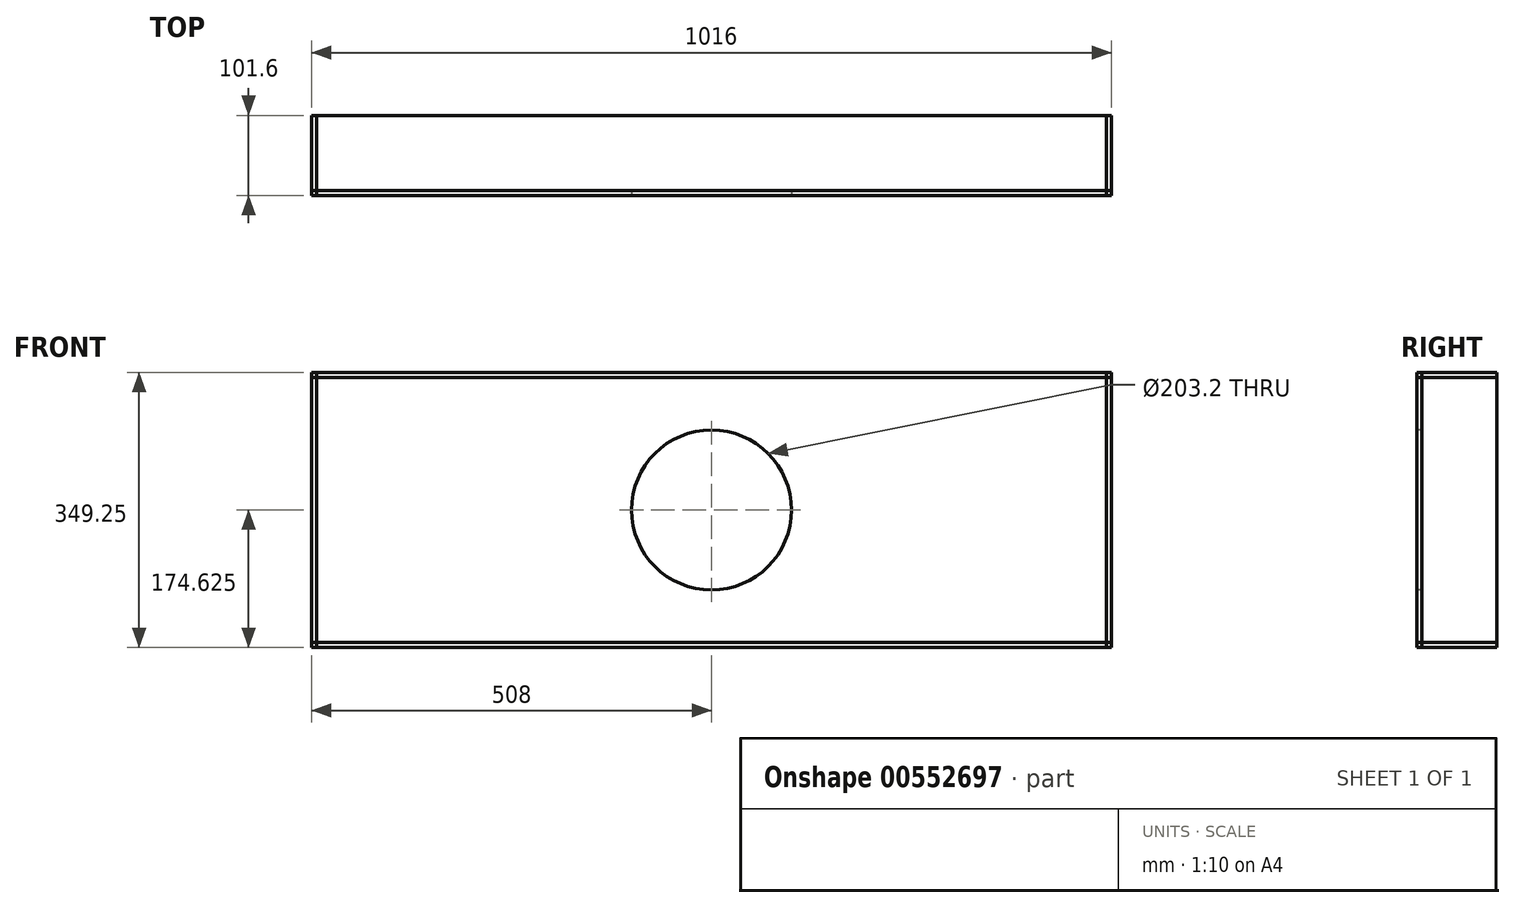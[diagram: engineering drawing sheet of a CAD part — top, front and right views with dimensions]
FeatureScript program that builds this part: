
annotation { "Feature Type Name" : "Feature", "Feature Type Description" : "" }
export const myFeature = defineFeature(function(context is Context, id is Id, definition is map)
    precondition{}
    {
        {
            var Q0;
            Q0=qCreatedBy(makeId("Front.planeOp"),FACE);
            var sketch = newSketch(context, id + "F0", { "sketchPlane" : qUnion([Q0])});
            skLineSegment(sketch, "E0.bottom", {"start": v(0, 0) * mm, "end": v(1016, 0) * mm});
            skLineSegment(sketch, "E0.top", {"start": v(0, 349.25) * mm, "end": v(1016, 349.25) * mm});
            skLineSegment(sketch, "E0.left", {"start": v(0, 0) * mm, "end": v(0, 349.25) * mm});
            skLineSegment(sketch, "E0.right", {"start": v(1016, 0) * mm, "end": v(1016, 349.25) * mm});
            skCircle(sketch, "E1", {"center": v(508, 174.62) * mm, "radius": 101.6 * mm});
            skLineSegment(sketch, "E2", {"start": v(508, 174.62) * mm, "end": v(1016, 174.62) * mm, "construction": true});
            skLineSegment(sketch, "E3", {"start": v(508, 174.62) * mm, "end": v(508, 349.25) * mm, "construction": true});
            skSolve(sketch);
        }
        {
            var Q0;
            Q0=makeQuery(id+"F0.imprint","IMPRINT",FACE,{"disambiguationData":[TD([[makeQuery(id+"F0.imprint","IMPRINT",EDGE,{"derivedFrom":sQuery(id+"F0.wireOp",EDGE,"E0.bottom")}),1.0]])]});
            extrude(context, id + "F1", {"entities" : qUnion([Q0]), "oppositeDirection" : true, "depth" : 6.35 * mm, "offsetDistance" : 25.4 * mm});
        }
        {
            var Q0;
            Q0=qCreatedBy(makeId("Front.planeOp"),FACE);
            var sketch = newSketch(context, id + "F2", { "sketchPlane" : qUnion([Q0])});
            skLineSegment(sketch, "E4.bottom", {"start": v(0, 349.25) * mm, "end": v(1016, 349.25) * mm});
            skLineSegment(sketch, "E4.top", {"start": v(0, 342.9) * mm, "end": v(1016, 342.9) * mm});
            skLineSegment(sketch, "E4.left", {"start": v(0, 342.9) * mm, "end": v(0, 349.25) * mm});
            skLineSegment(sketch, "E4.right", {"start": v(1016, 342.9) * mm, "end": v(1016, 349.25) * mm});
            skSolve(sketch);
        }
        {
            var Q0;
            Q0=makeQuery(id+"F2.imprint","IMPRINT",FACE,{"disambiguationData":[TD([[makeQuery(id+"F2.imprint","IMPRINT",EDGE,{"derivedFrom":sQuery(id+"F2.wireOp",EDGE,"E4.bottom")}),-1.0]])]});
            extrude(context, id + "F3", {"entities" : qUnion([Q0]), "oppositeDirection" : true, "depth" : 101.6 * mm, "offsetDistance" : 25.4 * mm});
        }
        {
            var Q0;
            Q0=makeQuery(id+"F3.opExtrude","SWEPT_FACE",FACE,{"disambiguationData":[OSD([sQuery(id+"F2.wireOp",EDGE,"E4.bottom")])]});
            var sketch = newSketch(context, id + "F4", { "sketchPlane" : qUnion([Q0])});
            skLineSegment(sketch, "E5.bottom", {"start": v(1016, 101.6) * mm, "end": v(1009.65, 101.6) * mm});
            skLineSegment(sketch, "E5.top", {"start": v(1016, 0) * mm, "end": v(1009.65, 0) * mm});
            skLineSegment(sketch, "E5.left", {"start": v(1016, 101.6) * mm, "end": v(1016, 0) * mm});
            skLineSegment(sketch, "E5.right", {"start": v(1009.65, 101.6) * mm, "end": v(1009.65, 0) * mm});
            skSolve(sketch);
        }
        {
            var Q0;
            Q0=makeQuery(id+"F4.imprint","IMPRINT",FACE,{"disambiguationData":[TD([[makeQuery(id+"F4.imprint","IMPRINT",EDGE,{"derivedFrom":sQuery(id+"F4.wireOp",EDGE,"E5.bottom")}),-1.0]])]});
            var Q1;
            Q1=makeQuery(id+"F1.opExtrude","CAP_VERTEX",VERTEX,{"disambiguationData":[OSD([sQuery(id+"F0.wireOp",EDGE,"E0.bottom"),sQuery(id+"F0.wireOp",EDGE,"E0.right")])],"isStart":false});
            extrude(context, id + "F5", {"entities" : qUnion([Q0]), "endBound" : BoundingType.UP_TO_VERTEX, "oppositeDirection" : true, "depth" : 25.4 * mm, "endBoundEntityVertex" : qUnion([Q1]), "offsetDistance" : 25.4 * mm});
        }
        {
            var Q0;
            Q0=makeQuery(id+"F3.opExtrude","SWEPT_BODY",BODY,{"disambiguationData":[OSD([sQuery(id+"F2.wireOp",EDGE,"E4.bottom"),sQuery(id+"F2.wireOp",EDGE,"E4.top"),sQuery(id+"F2.wireOp",EDGE,"E4.left"),sQuery(id+"F2.wireOp",EDGE,"E4.right")])]});
            transform(context, id + "F6", {"entities" : qUnion([Q0]), "transformType" : TransformType.TRANSLATION_3D, "dx" : 0 * mm, "dy" : 0 * mm, "dz" : -342.9 * mm, "makeCopy" : true});
        }
        {
            var Q0;
            Q0=makeQuery(id+"F5.opExtrude","SWEPT_BODY",BODY,{"disambiguationData":[OSD([sQuery(id+"F4.wireOp",EDGE,"E5.bottom"),sQuery(id+"F4.wireOp",EDGE,"E5.top"),sQuery(id+"F4.wireOp",EDGE,"E5.left"),sQuery(id+"F4.wireOp",EDGE,"E5.right")])]});
            transform(context, id + "F7", {"entities" : qUnion([Q0]), "transformType" : TransformType.TRANSLATION_3D, "dx" : -1009.65 * mm, "dy" : 0 * mm, "dz" : 0 * mm, "makeCopy" : true});
        }
    });
